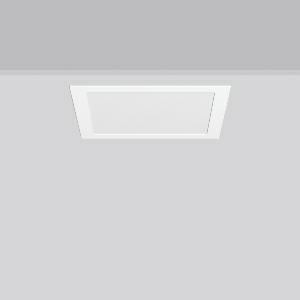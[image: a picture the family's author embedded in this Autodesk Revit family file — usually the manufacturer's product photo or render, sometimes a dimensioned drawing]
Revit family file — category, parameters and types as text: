
# Revit family: toledo_flat_square_e_901671_002_76_d94b
name_source: partatom
category: Lighting Fixtures
units: mm (PartAtom-declared; Revit-internal decimal feet)

## family parameters
Cut with Voids When Loaded = No
Host = Face
Light Source = No
Part Type = Normal
Room Calculation Point = No
Round Connector Dimension = Use Diameter
Shared = No

## types (1)
- TuneableWhite 846 (1 x LED Modul 846, 2400 lm, 4600)
    Apparent Load = 24 VA
    CIE Flux Codes = 47 79 96 100 100
    Color Rendering = 80
    Color Temperature = 4600
    Default Elevation = 1800 mm
    Description = Series: TOLEDO FLAT square
Ultra thin recessed downlight. Housing: die-cast aluminium. Light guide and diffuser made of non-yellowing PMMA, opal matt. Tunable white dynamically adjustable from 2700 K to 6500 K. Ceiling installation with spring system. Mounting depth depends on ceiling strength. Surface mounted housing as accessory for all sizes. Retrofittable decorative cylinders made of chintz fabric as accessory, optional with satin finish plastic diffuser. Through-wiring box (5 pole) available as accessory. 
Colour: white
Length: 300 mm
Width: 300 mm
Height: 3 mm
Cut-out length: 280 mm
Cut-out width: 280 mm
Recess height: 31-56 mm
Luminaire: recess height: 31-51 mm
Lamp: LED
Socket: without socket
Colour temperature: 2700K - 6500K
Colour rendering index (CRI): 80
System power: 24 W
Rated luminous flux: 2400 lm
Luminous efficiency: 100 lm/W
System power 2: 26 W
Rated luminous flux 2: 2200 lm
Luminous efficiency 2: 85 lm/W
System power 3: 24 W
Rated luminous flux 3: 2350 lm
Luminous efficiency 3: 98 lm/W
Control gear: Converter, dimmable, DALI
Protection class: II
Type of protection: IP 54
    Height = 0 mm  [stored 0 ft]
    Lamp = 1 x LED Modul 846
    Lamp Light Flux = 2400 lm
    Lamp count = 1
    Length = 300 mm
    Lifetime = 50000 h
    Luminous efficacy = 100 lm/W
    Manufacturer = RZB
    ModVariant = No
    Model = 901671.002.76
    Mounting Place = Ceiling
    Mounting Type = Recessed
    Number of Poles = 1
    OnlyDefault = Yes
    Power Factor = 1
    Product Name = TOLEDO FLAT square E
    Product group = Recessed downlights
    ProductGroupID = 402
    Protection Class = Protection class II
    Protection Degree = IP 20
    RLX_Detail_Level = 1
    RLX_Emergency_Light_Flux = 0 lm
    RLX_Emergency_Type = 0
    RLX_Emergency_Type_DB = No
    RlxData = <blob elided: 60789 chars, md5=cabddae3>
    Socket = socket
    Standby Power = 0 W
    System Light Flux = 2400 lm
    System Power = 24 W
    Type Comments = TuneableWhite 846
    Type Image = 901488.002.jpg
    URL = http://relux.com
    VarID = tuneablewhite_846
    Voltage = 230 V
    Voltage Range = 220-240 V
    Weight = 0.00 kg
    Width = 300 mm

note: [stored X ft] marks values corroborated as IEEE doubles in the binary element streams (Revit-internal decimal feet)

## geometry (parser evidence)
native form markers: Blend x4, Sweep x13
no freeform markers — native parametric forms only
